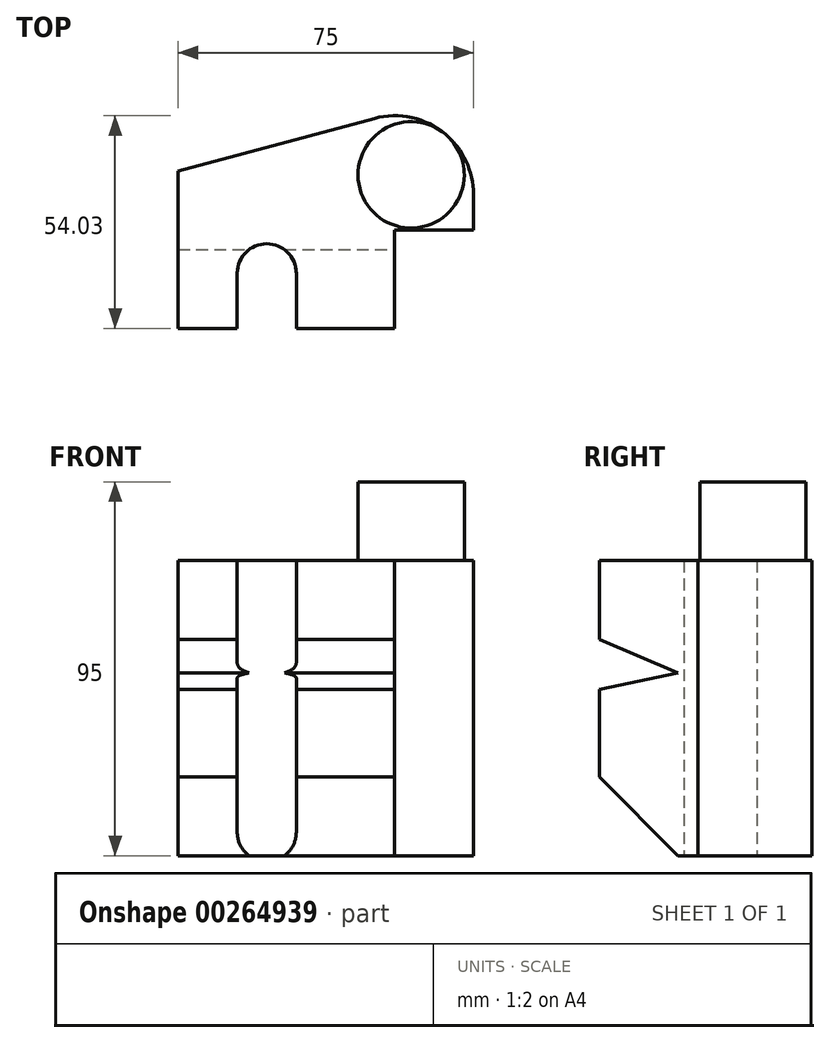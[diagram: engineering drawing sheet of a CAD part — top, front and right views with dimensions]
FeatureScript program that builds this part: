
annotation { "Feature Type Name" : "Feature", "Feature Type Description" : "" }
export const myFeature = defineFeature(function(context is Context, id is Id, definition is map)
    precondition{}
    {
        {
            var Q0;
            Q0=qCreatedBy(makeId("Top.planeOp"),FACE);
            var sketch = newSketch(context, id + "F0", { "sketchPlane" : qUnion([Q0])});
            skLineSegment(sketch, "E0", {"start": v(0, 0) * mm, "end": v(15, 0) * mm});
            skLineSegment(sketch, "E1", {"start": v(15, 0) * mm, "end": v(15, 14) * mm});
            skLineSegment(sketch, "E2", {"start": v(30, 14) * mm, "end": v(30, 0) * mm});
            skLineSegment(sketch, "E3", {"start": v(55, 0) * mm, "end": v(55, 25) * mm});
            skLineSegment(sketch, "E4", {"start": v(55, 25) * mm, "end": v(75, 25) * mm});
            skLineSegment(sketch, "E5", {"start": v(75, 25) * mm, "end": v(75, 34.03) * mm});
            skLineSegment(sketch, "E6", {"start": v(49.82, 53.35) * mm, "end": v(0, 40) * mm});
            skLineSegment(sketch, "E7", {"start": v(0, 40) * mm, "end": v(0, 0) * mm});
            skPoint(sketch, "E8.visualSharp", {"position": v(75, 60.1) * mm});
            skArc(sketch, "E8.filletArc", {"start": v(75, 34.03) * mm, "mid": v(67.18, 49.9) * mm, "end": v(49.82, 53.35) * mm});
            skLineSegment(sketch, "E9", {"start": v(30, 0) * mm, "end": v(55, 0) * mm});
            skArc(sketch, "E10", {"start": v(15, 14) * mm, "mid": v(22.5, 21.5) * mm, "end": v(30, 14) * mm});
            skSolve(sketch);
        }
        {
            var Q0;
            Q0 = qSketchRegion(id + "F0", true);
            extrude(context, id + "F1", {"entities" : qUnion([Q0]), "depth" : 75 * mm});
        }
        {
            var Q0;
            Q0=makeQuery(id+"F1.opExtrude","SWEPT_FACE",FACE,{"disambiguationData":[OSD([sQuery(id+"F0.wireOp",EDGE,"E3")])]});
            var sketch = newSketch(context, id + "F2", { "sketchPlane" : qUnion([Q0])});
            skLineSegment(sketch, "E11", {"start": v(0, 55) * mm, "end": v(20, 46.44) * mm});
            skLineSegment(sketch, "E12", {"start": v(20, 46.44) * mm, "end": v(0, 42.25) * mm});
            skLineSegment(sketch, "E13", {"start": v(0, 20) * mm, "end": v(20, 0) * mm});
            skLineSegment(sketch, "E14", {"start": v(0, 42.25) * mm, "end": v(0, 55) * mm});
            skLineSegment(sketch, "E15", {"start": v(0, 20) * mm, "end": v(0, 0) * mm});
            skLineSegment(sketch, "E16", {"start": v(0, 0) * mm, "end": v(20, 0) * mm});
            skSolve(sketch);
        }
        {
            var Q0;
            Q0 = qSketchRegion(id + "F2", true);
            extrude(context, id + "F3", {"entities" : qUnion([Q0]), "operationType" : NewBodyOperationType.REMOVE, "endBound" : BoundingType.THROUGH_ALL, "oppositeDirection" : true, "depth" : 25 * mm});
        }
        {
            var Q0;
            Q0=makeQuery(id+"F1.opExtrude","CAP_FACE",FACE,{"disambiguationData":[OSD([sQuery(id+"F0.wireOp",EDGE,"E0"),sQuery(id+"F0.wireOp",EDGE,"E1"),sQuery(id+"F0.wireOp",EDGE,"E2"),sQuery(id+"F0.wireOp",EDGE,"E3"),sQuery(id+"F0.wireOp",EDGE,"E4"),sQuery(id+"F0.wireOp",EDGE,"E5"),sQuery(id+"F0.wireOp",EDGE,"E6"),sQuery(id+"F0.wireOp",EDGE,"E7"),sQuery(id+"F0.wireOp",EDGE,"E8.filletArc"),sQuery(id+"F0.wireOp",EDGE,"E9"),sQuery(id+"F0.wireOp",EDGE,"E10")])],"isStart":false});
            var sketch = newSketch(context, id + "F4", { "sketchPlane" : qUnion([Q0])});
            skCircle(sketch, "E17", {"center": v(59.2, 39) * mm, "radius": 13.5 * mm});
            skSolve(sketch);
        }
        {
            var Q0;
            Q0 = qSketchRegion(id + "F4", true);
            extrude(context, id + "F5", {"entities" : qUnion([Q0]), "operationType" : NewBodyOperationType.ADD, "depth" : 20 * mm});
        }
    });
